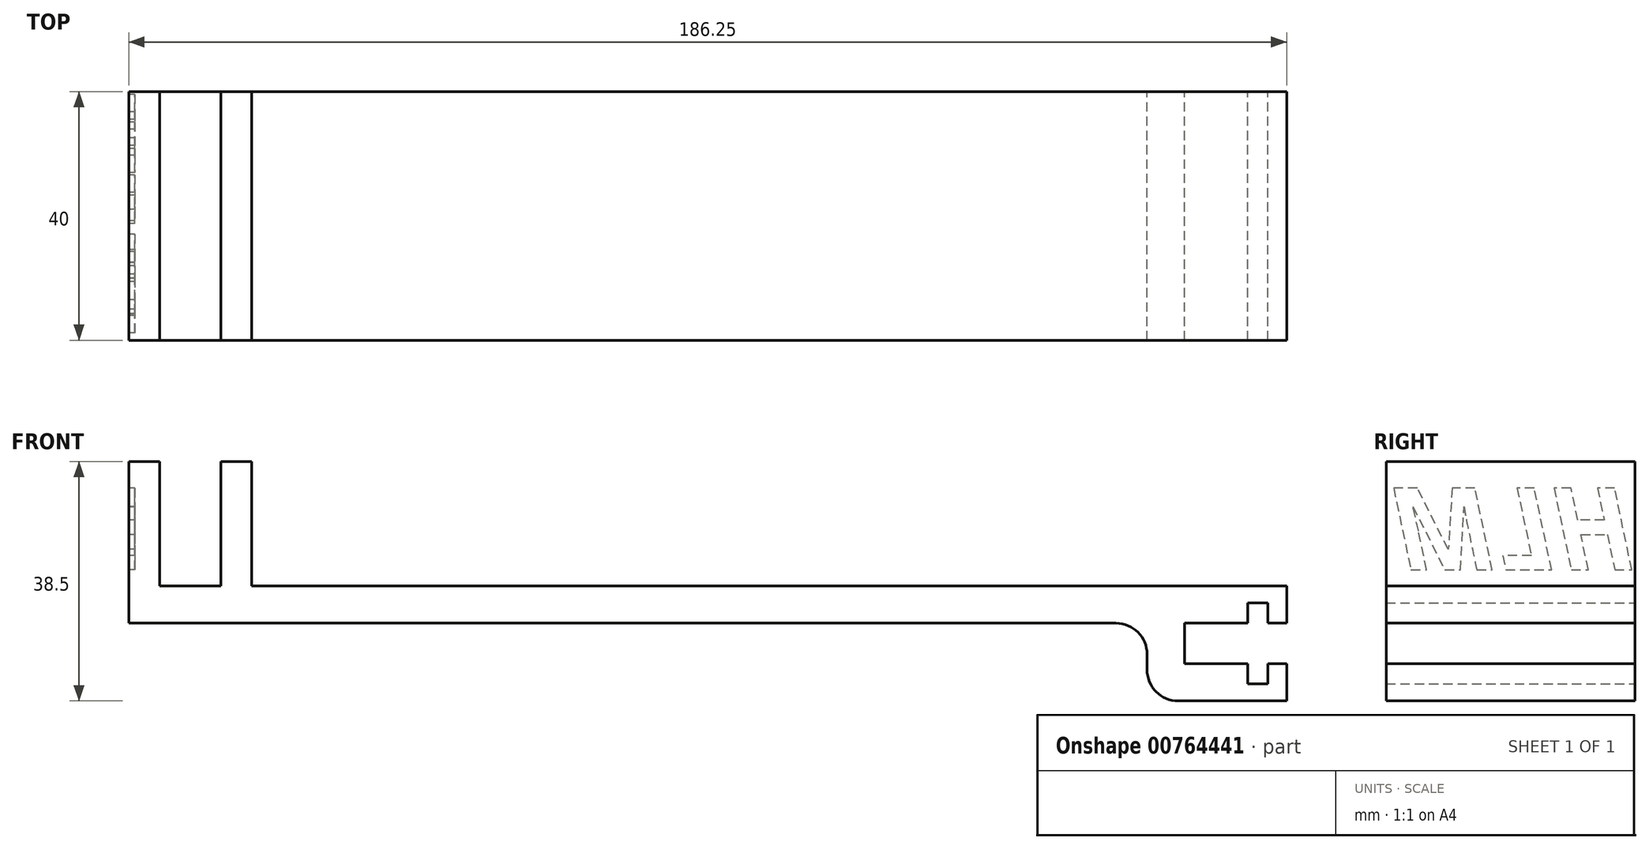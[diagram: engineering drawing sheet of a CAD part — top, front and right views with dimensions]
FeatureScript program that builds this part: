
annotation { "Feature Type Name" : "Feature", "Feature Type Description" : "" }
export const myFeature = defineFeature(function(context is Context, id is Id, definition is map)
    precondition{}
    {
        {
            assignVariable(context, id + "F0", {"name" : "Latime_brat", "anyValue" : 40});
        }
        {
            var Q0;
            Q0=qCreatedBy(makeId("Front.planeOp"),FACE);
            var sketch = newSketch(context, id + "F1", { "sketchPlane" : qUnion([Q0])});
            skLineSegment(sketch, "E0", {"start": v(-186.25, 12.5) * mm, "end": v(-186.25, 38.5) * mm});
            skLineSegment(sketch, "E1", {"start": v(-186.25, 38.5) * mm, "end": v(-181.25, 38.5) * mm});
            skLineSegment(sketch, "E2", {"start": v(-181.25, 38.5) * mm, "end": v(-181.25, 18.5) * mm});
            skLineSegment(sketch, "E3", {"start": v(-181.25, 18.5) * mm, "end": v(-171.45, 18.5) * mm});
            skLineSegment(sketch, "E4", {"start": v(-171.45, 18.5) * mm, "end": v(-171.45, 38.5) * mm});
            skLineSegment(sketch, "E5", {"start": v(-171.45, 38.5) * mm, "end": v(-166.45, 38.5) * mm});
            skLineSegment(sketch, "E6", {"start": v(-166.45, 38.5) * mm, "end": v(-166.45, 18.5) * mm});
            skLineSegment(sketch, "E7", {"start": v(-166.45, 18.5) * mm, "end": v(0, 18.5) * mm});
            skLineSegment(sketch, "E8", {"start": v(0, 18.5) * mm, "end": v(0, 12.5) * mm});
            skLineSegment(sketch, "E9", {"start": v(0, 12.5) * mm, "end": v(-3, 12.5) * mm});
            skLineSegment(sketch, "E10", {"start": v(-3, 12.5) * mm, "end": v(-3, 15.75) * mm});
            skLineSegment(sketch, "E11", {"start": v(-3, 15.75) * mm, "end": v(-6.25, 15.75) * mm});
            skLineSegment(sketch, "E12", {"start": v(-6.25, 15.75) * mm, "end": v(-6.25, 12.5) * mm});
            skLineSegment(sketch, "E13", {"start": v(-6.25, 12.5) * mm, "end": v(-16.45, 12.5) * mm});
            skLineSegment(sketch, "E14", {"start": v(-16.45, 12.5) * mm, "end": v(-16.45, 6) * mm});
            skLineSegment(sketch, "E15", {"start": v(-16.45, 6) * mm, "end": v(-6.25, 6) * mm});
            skLineSegment(sketch, "E16", {"start": v(-6.25, 6) * mm, "end": v(-6.25, 2.75) * mm});
            skLineSegment(sketch, "E17", {"start": v(-6.25, 2.75) * mm, "end": v(-3, 2.75) * mm});
            skLineSegment(sketch, "E18", {"start": v(-3, 2.75) * mm, "end": v(-3, 6) * mm});
            skLineSegment(sketch, "E19", {"start": v(-3, 6) * mm, "end": v(0, 6) * mm});
            skLineSegment(sketch, "E20", {"start": v(0, 6) * mm, "end": v(0, 0) * mm});
            skLineSegment(sketch, "E21", {"start": v(-186.25, 12.5) * mm, "end": v(-27.45, 12.5) * mm});
            skLineSegment(sketch, "E22", {"start": v(-22.45, 7.5) * mm, "end": v(-22.45, 5) * mm});
            skLineSegment(sketch, "E23", {"start": v(-17.45, 0) * mm, "end": v(0, 0) * mm});
            skPoint(sketch, "E24.visualSharp", {"position": v(-22.45, 12.5) * mm});
            skArc(sketch, "E24.filletArc", {"start": v(-22.45, 7.5) * mm, "mid": v(-23.91, 11.04) * mm, "end": v(-27.45, 12.5) * mm});
            skPoint(sketch, "E25.visualSharp", {"position": v(-22.45, 0) * mm});
            skArc(sketch, "E25.filletArc", {"start": v(-22.45, 5) * mm, "mid": v(-20.99, 1.46) * mm, "end": v(-17.45, 0) * mm});
            skLineSegment(sketch, "E26", {"start": v(-166.45, 18.5) * mm, "end": v(-166.45, 12.5) * mm, "construction": true});
            skSolve(sketch);
        }
        {
            var Q0;
            Q0=makeQuery(id+"F1.imprint","IMPRINT",FACE,{"disambiguationData":[TD([[makeQuery(id+"F1.imprint","IMPRINT",EDGE,{"derivedFrom":sQuery(id+"F1.wireOp",EDGE,"E0")}),-1.0]])]});
            extrude(context, id + "F2", {"entities" : qUnion([Q0]), "depth" : getVariable(context, 'Latime_brat') * mm, "offsetDistance" : 25 * mm});
        }
        {
            var Q0;
            Q0=makeQuery(id+"F2.opExtrude","SWEPT_FACE",FACE,{"disambiguationData":[OSD([sQuery(id+"F1.wireOp",EDGE,"E0")])]});
            var sketch = newSketch(context, id + "F3", { "sketchPlane" : qUnion([Q0])});
            skText(sketch, "E27", { "text": "HLM\n", "fontName": "OpenSans-BoldItalic.ttf"});
            const initialGuessF3  = {"E27": [0, 0.02107, 1, 0, 0.01328]};
            skSetInitialGuess(sketch, initialGuessF3);
            skSolve(sketch);
        }
        {
            var Q0;
            Q0 = qSketchRegion(id + "F3", true);
            extrude(context, id + "F4", {"entities" : qUnion([Q0]), "operationType" : NewBodyOperationType.REMOVE, "oppositeDirection" : true, "depth" : 1 * mm, "offsetDistance" : 25 * mm});
        }
    });
